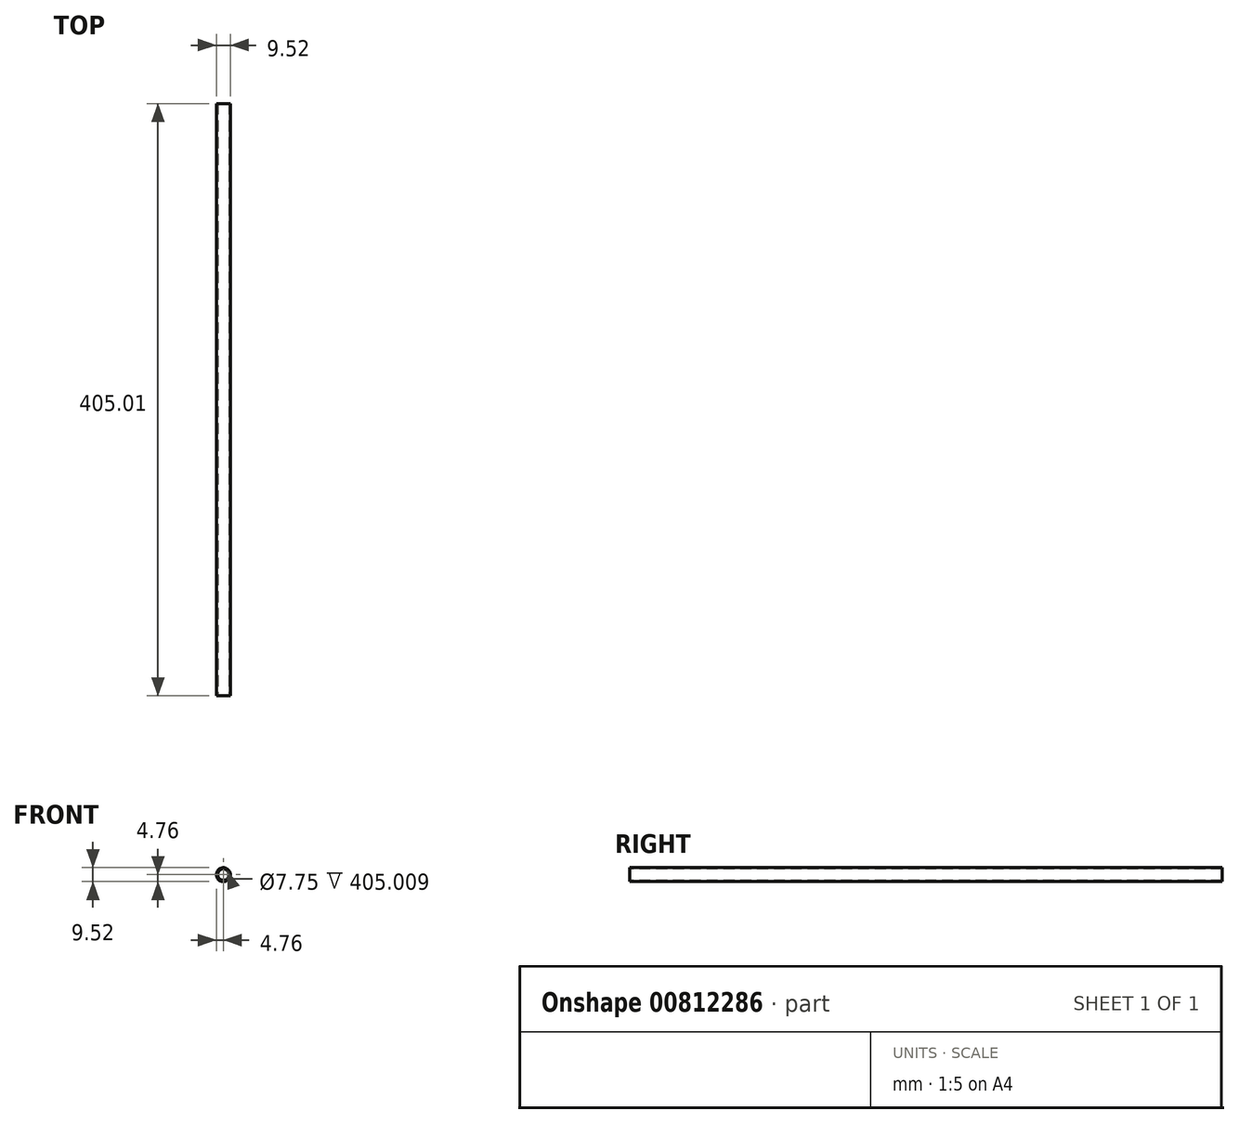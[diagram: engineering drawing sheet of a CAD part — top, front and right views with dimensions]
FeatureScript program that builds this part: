
annotation { "Feature Type Name" : "Feature", "Feature Type Description" : "" }
export const myFeature = defineFeature(function(context is Context, id is Id, definition is map)
    precondition{}
    {
        {
            var Q0;
            Q0=qCreatedBy(makeId("Front.planeOp"),FACE);
            var sketch = newSketch(context, id + "F0", { "sketchPlane" : qUnion([Q0])});
            skCircle(sketch, "E0", {"center": v(0, 0) * mm, "radius": 4.76 * mm});
            skCircle(sketch, "E1", {"center": v(0, 0) * mm, "radius": 3.87 * mm});
            skLineSegment(sketch, "E2", {"start": v(0, 0) * mm, "end": v(14.13, 0) * mm});
            skSolve(sketch);
        }
        {
            var Q0;
            Q0=makeQuery(id+"F0.imprint","IMPRINT",FACE,{"disambiguationData":[TD([[makeQuery(id+"F0.imprint","IMPRINT",EDGE,{"derivedFrom":sQuery(id+"F0.wireOp",EDGE,"E0")}),1.0]])]});
            var Q1;
            Q1=sQuery(id+"F0.wireOp",EDGE,"E0");
            extrude(context, id + "F1", {"entities" : qUnion([Q0]), "surfaceEntities" : qUnion([Q1]), "depth" : -405 * mm, "offsetDistance" : 25.4 * mm});
        }
        {
            var Q0;
            Q0=makeQuery(id+"F1.opExtrude","SWEPT_BODY",BODY,{"disambiguationData":[OSD([sQuery(id+"F0.wireOp",EDGE,"E0"),sQuery(id+"F0.wireOp",EDGE,"E1")])]});
            var Q1;
            Q1=makeQuery(id+"F1.opExtrude","SWEPT_FACE",FACE,{"disambiguationData":[OSD([sQuery(id+"F0.wireOp",EDGE,"E1")])]});
            transform(context, id + "F2", {"entities" : qUnion([Q0]), "transformType" : TransformType.ROTATION, "transformAxis" : qUnion([Q1]), "angle" : 30 * degree, "makeCopy" : false});
        }
        {
            var Q0;
            Q0=makeQuery(id+"F1.opExtrude","SWEPT_BODY",BODY,{"disambiguationData":[OSD([sQuery(id+"F0.wireOp",EDGE,"E0"),sQuery(id+"F0.wireOp",EDGE,"E1")])]});
            var Q1;
            Q1=makeQuery(id+"F1.opExtrude","SWEPT_FACE",FACE,{"disambiguationData":[OSD([sQuery(id+"F0.wireOp",EDGE,"E0")])]});
            transform(context, id + "F3", {"entities" : qUnion([Q0]), "transformType" : TransformType.ROTATION, "transformAxis" : qUnion([Q1]), "angle" : 30 * degree, "makeCopy" : false});
        }
    });
